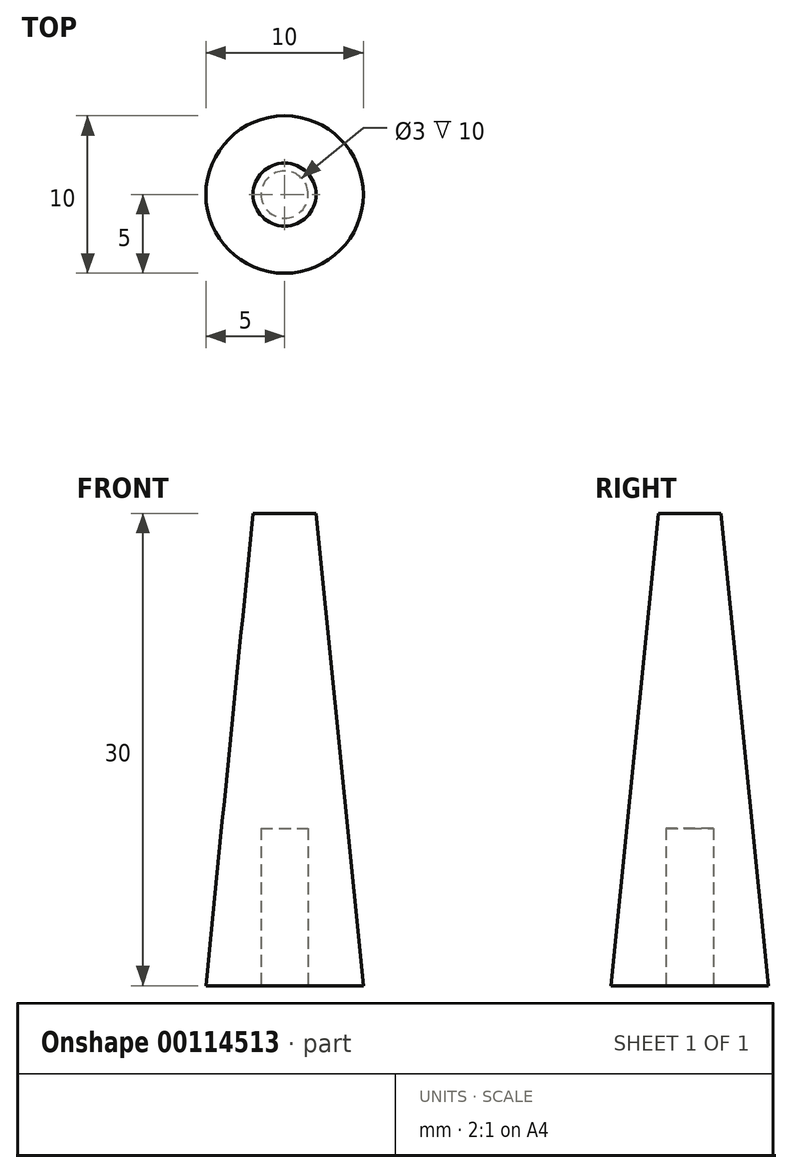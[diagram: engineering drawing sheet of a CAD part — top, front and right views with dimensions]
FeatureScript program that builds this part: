
annotation { "Feature Type Name" : "Feature", "Feature Type Description" : "" }
export const myFeature = defineFeature(function(context is Context, id is Id, definition is map)
    precondition{}
    {
        {
            var Q0;
            Q0=qCreatedBy(makeId("Front.planeOp"),FACE);
            var sketch = newSketch(context, id + "F0", { "sketchPlane" : qUnion([Q0])});
            skLineSegment(sketch, "E0", {"start": v(-1.5, 0) * mm, "end": v(-1.5, 10) * mm});
            skLineSegment(sketch, "E1", {"start": v(-1.5, 10) * mm, "end": v(0, 10) * mm});
            skLineSegment(sketch, "E2", {"start": v(0, 10) * mm, "end": v(0, 30) * mm});
            skLineSegment(sketch, "E3", {"start": v(0, 30) * mm, "end": v(-2, 30) * mm});
            skLineSegment(sketch, "E4", {"start": v(-2, 30) * mm, "end": v(-5, 0) * mm});
            skLineSegment(sketch, "E5", {"start": v(-5, 0) * mm, "end": v(-1.5, 0) * mm});
            skSolve(sketch);
        }
        {
            var Q0;
            Q0=makeQuery(id+"F0.imprint","IMPRINT",FACE,{"disambiguationData":[TD([[makeQuery(id+"F0.imprint","IMPRINT",EDGE,{"derivedFrom":sQuery(id+"F0.wireOp",EDGE,"E0")}),1.0]])]});
            var Q1;
            Q1=sQuery(id+"F0.wireOp",EDGE,"E2");
            revolve(context, id + "F1", {"entities" : qUnion([Q0]), "axis" : qUnion([Q1]), "revolveType" : RevolveType.FULL});
        }
    });
